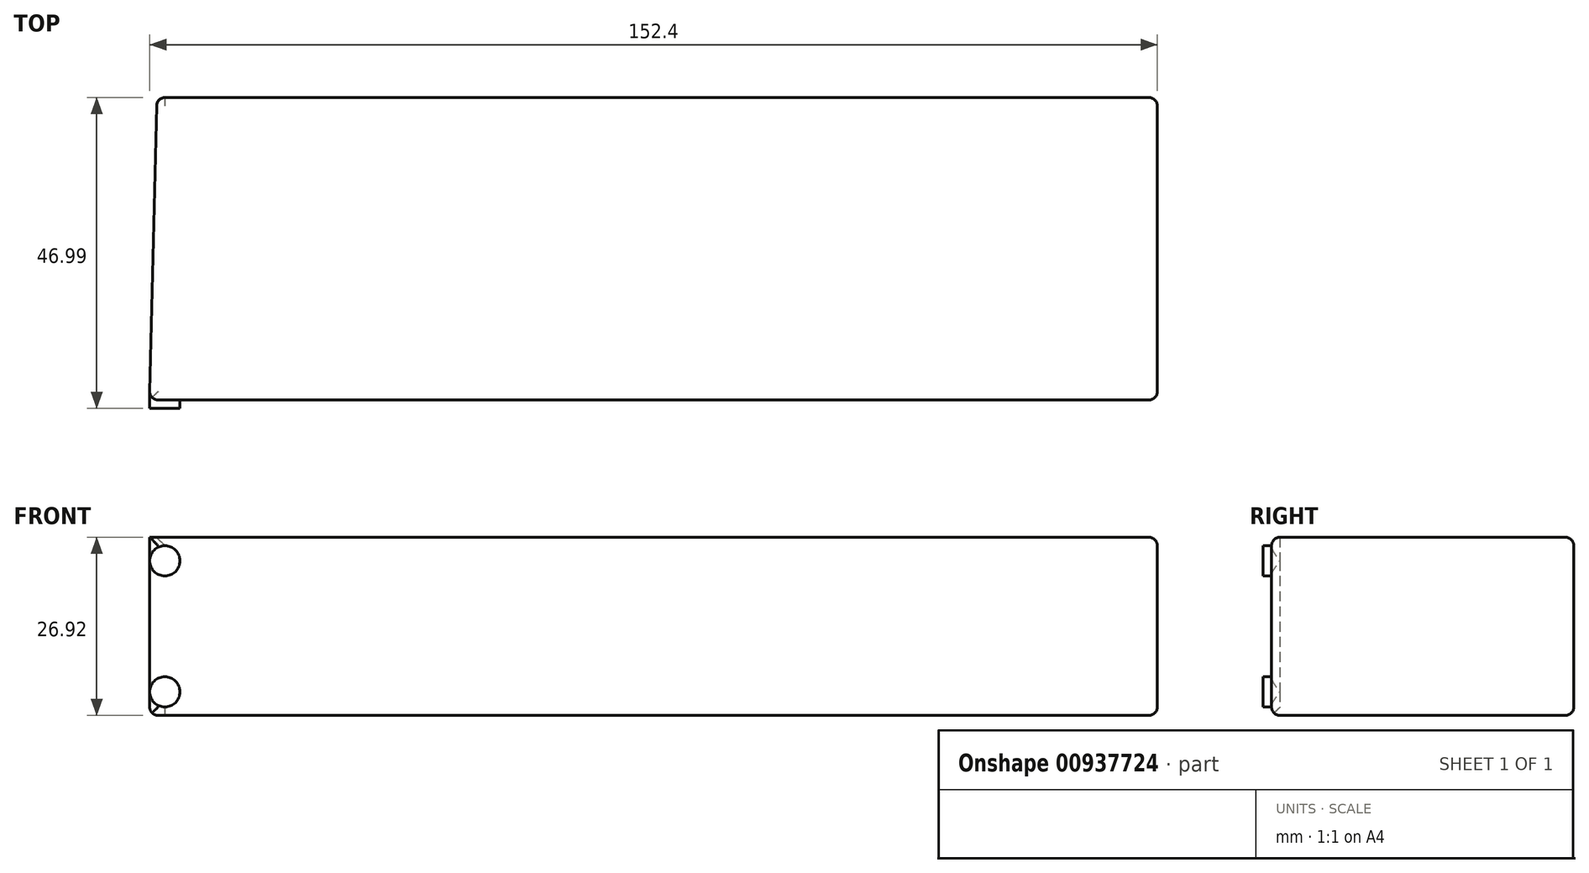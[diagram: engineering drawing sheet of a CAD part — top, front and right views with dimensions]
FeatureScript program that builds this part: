
annotation { "Feature Type Name" : "Feature", "Feature Type Description" : "" }
export const myFeature = defineFeature(function(context is Context, id is Id, definition is map)
    precondition{}
    {
        {
            var Q0;
            Q0=qCreatedBy(makeId("Right.planeOp"),FACE);
            var sketch = newSketch(context, id + "F0", { "sketchPlane" : qUnion([Q0])});
            skLineSegment(sketch, "E0.bottom", {"start": v(-22.86, 13.46) * mm, "end": v(22.86, 13.46) * mm});
            skLineSegment(sketch, "E0.top", {"start": v(-22.86, -13.46) * mm, "end": v(22.86, -13.46) * mm});
            skLineSegment(sketch, "E0.left", {"start": v(-22.86, 13.46) * mm, "end": v(-22.86, -13.46) * mm});
            skLineSegment(sketch, "E0.right", {"start": v(22.86, 13.46) * mm, "end": v(22.86, -13.46) * mm});
            skLineSegment(sketch, "E1", {"start": v(22.86, -13.46) * mm, "end": v(-22.86, 13.46) * mm, "construction": true});
            skLineSegment(sketch, "E2", {"start": v(22.86, 13.46) * mm, "end": v(-22.86, -13.46) * mm, "construction": true});
            skSolve(sketch);
        }
        {
            var Q0;
            Q0=makeQuery(id+"F0.imprint","IMPRINT",FACE,{"disambiguationData":[TD([[makeQuery(id+"F0.imprint","IMPRINT",EDGE,{"derivedFrom":sQuery(id+"F0.wireOp",EDGE,"E0.bottom")}),-1.0]])]});
            extrude(context, id + "F1", {"entities" : qUnion([Q0]), "endBound" : BoundingType.SYMMETRIC, "depth" : 152.4 * mm, "offsetDistance" : 25.4 * mm});
        }
        {
            var Q0;
            Q0=makeQuery(id+"F1.opExtrude","SWEPT_FACE",FACE,{"disambiguationData":[OSD([sQuery(id+"F0.wireOp",EDGE,"E0.left")])]});
            var Q1;
            Q1=makeQuery(id+"F1.opExtrude","SWEPT_FACE",FACE,{"disambiguationData":[OSD([sQuery(id+"F0.wireOp",EDGE,"E0.right")])]});
            var Q2;
            Q2=makeQuery(id+"F1.opExtrude","CAP_EDGE",EDGE,{"disambiguationData":[OSD([sQuery(id+"F0.wireOp",EDGE,"E0.bottom")])],"isStart":false});
            var Q3;
            Q3=makeQuery(id+"F1.opExtrude","CAP_EDGE",EDGE,{"disambiguationData":[OSD([sQuery(id+"F0.wireOp",EDGE,"E0.top")])],"isStart":false});
            fillet(context, id + "F2", {"entities" : qUnion([Q0, Q1, Q2, Q3]), "radius" : 1.27 * mm, "tangentPropagation" : true, "allowEdgeOverflow" : false});
        }
        {
            var Q0;
            Q0=makeQuery(id+"F1.opExtrude","SWEPT_FACE",FACE,{"disambiguationData":[OSD([sQuery(id+"F0.wireOp",EDGE,"E0.bottom")])]});
            var sketch = newSketch(context, id + "F3", { "sketchPlane" : qUnion([Q0])});
            skLineSegment(sketch, "E3.0.0", {"start": v(74.93, 22.86) * mm, "end": v(-74.93, 22.86) * mm, "construction": true});
            skLineSegment(sketch, "E3.0.2", {"start": v(-74.93, 22.86) * mm, "end": v(74.93, 22.86) * mm, "construction": true});
            skLineSegment(sketch, "E4.0.0", {"start": v(74.93, -22.86) * mm, "end": v(-74.93, -22.86) * mm, "construction": true});
            skLineSegment(sketch, "E4.0.2", {"start": v(-74.93, -22.86) * mm, "end": v(74.93, -22.86) * mm, "construction": true});
            skArc(sketch, "E5.0.0", {"start": v(-74.93, -22.86) * mm, "mid": v(-75.83, -22.49) * mm, "end": v(-76.2, -21.59) * mm, "construction": true});
            skArc(sketch, "E5.0.2", {"start": v(-76.2, -21.59) * mm, "mid": v(-75.83, -22.49) * mm, "end": v(-74.93, -22.86) * mm, "construction": true});
            skLineSegment(sketch, "E6.0.0", {"start": v(-76.2, -21.59) * mm, "end": v(-76.2, 21.59) * mm, "construction": true});
            skLineSegment(sketch, "E6.0.2", {"start": v(-76.2, 21.59) * mm, "end": v(-76.2, -21.59) * mm, "construction": true});
            skArc(sketch, "E7.0.0", {"start": v(-76.2, 21.6) * mm, "mid": v(-75.83, 22.49) * mm, "end": v(-74.93, 22.86) * mm, "construction": true});
            skArc(sketch, "E7.0.2", {"start": v(-76.2, 21.59) * mm, "mid": v(-75.83, 22.49) * mm, "end": v(-74.93, 22.86) * mm, "construction": true});
            skArc(sketch, "E8.0.2", {"start": v(-76.2, 21.59) * mm, "mid": v(-75.83, 22.49) * mm, "end": v(-74.93, 22.86) * mm});
            skLineSegment(sketch, "E9.0.0", {"start": v(76.2, -21.6) * mm, "end": v(76.2, 21.59) * mm, "construction": true});
            skLineSegment(sketch, "E9.0.2", {"start": v(76.2, 21.6) * mm, "end": v(76.2, -21.59) * mm, "construction": true});
            skArc(sketch, "E10.0.0", {"start": v(74.93, 22.86) * mm, "mid": v(75.83, 22.49) * mm, "end": v(76.2, 21.6) * mm, "construction": true});
            skArc(sketch, "E10.0.2", {"start": v(76.2, 21.59) * mm, "mid": v(75.83, 22.49) * mm, "end": v(74.93, 22.86) * mm, "construction": true});
            skArc(sketch, "E11.0.0", {"start": v(76.2, -21.59) * mm, "mid": v(75.83, -22.49) * mm, "end": v(74.93, -22.86) * mm, "construction": true});
            skArc(sketch, "E11.0.2", {"start": v(74.93, -22.86) * mm, "mid": v(75.83, -22.49) * mm, "end": v(76.2, -21.59) * mm, "construction": true});
            skLineSegment(sketch, "E12", {"start": v(-75.13, 22.86) * mm, "end": v(-76.2, -21.6) * mm});
            skSolve(sketch);
        }
        {
            var Q0;
            {var subQ1=sQuery(id+"F0.wireOp",EDGE,"E0.bottom");var subQ2=makeQuery(id+"F1.opExtrude","CAP_EDGE",EDGE,{"disambiguationData":[OSD([subQ1])],"isStart":true});Q0=makeQuery(id+"F3.imprint","IMPRINT",FACE,{"disambiguationData":[TD([[makeQuery(id+"F3.imprint","IMPRINT",EDGE,{"derivedFrom":subQ2}),-1.0]])]});}
            var Q1;
            {var subQ0=sQuery(id+"F3.wireOp",EDGE,"E8.0.2");var subQ4=sQuery(id+"F3.wireOp",EDGE,"E12");var subQ5=makeQuery(id+"F3.imprint","INTERSECT",VERTEX,{"derivedFrom":[subQ0,subQ4]});Q1=makeQuery(id+"F3.imprint","IMPRINT",FACE,{"disambiguationData":[TD([[makeQuery(id+"F3.imprint","IMPRINT",EDGE,{"disambiguationData":[TD([[subQ5,-1.0]])],"derivedFrom":subQ4}),-1.0]])]});}
            extrude(context, id + "F4", {"entities" : qUnion([Q0, Q1]), "operationType" : NewBodyOperationType.REMOVE, "endBound" : BoundingType.THROUGH_ALL, "oppositeDirection" : true, "depth" : 25.4 * mm, "offsetDistance" : 25.4 * mm});
        }
        {
            var Q0;
            Q0=makeQuery(id+"F4.boolean.opBoolean","COPY",EDGE,{"derivedFrom":makeQuery(id+"F4.opExtrude","SWEPT_EDGE",EDGE,{"disambiguationData":[OSD([sQuery(id+"F3.wireOp",EDGE,"E8.0.2"),sQuery(id+"F3.wireOp",EDGE,"E12")])]})});
            var Q1;
            Q1=makeQuery(id+"F4.boolean.opBoolean","COPY",EDGE,{"derivedFrom":makeQuery(id+"F4.opExtrude","CAP_EDGE",EDGE,{"disambiguationData":[OSD([sQuery(id+"F3.wireOp",EDGE,"E12")])],"isStart":true})});
            var Q2;
            Q2=makeQuery(id+"F4.boolean.opBoolean","INTERSECT",EDGE,{"derivedFrom":[makeQuery(id+"F1.opExtrude","SWEPT_FACE",FACE,{"disambiguationData":[OSD([sQuery(id+"F0.wireOp",EDGE,"E0.top")])]}),makeQuery(id+"F4.opExtrude","SWEPT_FACE",FACE,{"disambiguationData":[OSD([sQuery(id+"F3.wireOp",EDGE,"E12")])]})]});
            fillet(context, id + "F5", {"entities" : qUnion([Q0, Q1, Q2]), "radius" : 1.27 * mm, "tangentPropagation" : true, "allowEdgeOverflow" : false});
        }
        {
            var Q0;
            Q0=makeQuery(id+"F1.opExtrude","SWEPT_FACE",FACE,{"disambiguationData":[OSD([sQuery(id+"F0.wireOp",EDGE,"E0.left")])]});
            var sketch = newSketch(context, id + "F6", { "sketchPlane" : qUnion([Q0])});
            skCircle(sketch, "E13", {"center": v(-73.91, 9.9) * mm, "radius": 2.29 * mm});
            skCircle(sketch, "E14", {"center": v(-73.91, -9.9) * mm, "radius": 2.29 * mm});
            skSolve(sketch);
        }
        {
            var Q0;
            {var subQ0=sQuery(id+"F6.wireOp",EDGE,"E13");var subQ1=sQuery(id+"F0.wireOp",EDGE,"E0.left");var subQ2=makeQuery(id+"F1.opExtrude","SWEPT_FACE",FACE,{"disambiguationData":[OSD([subQ1])]});var subQ3=makeQuery(id+"F2.opFillet","BLEND_EDGE",EDGE,{"blendedFrom":[makeQuery(id+"F1.opExtrude","CAP_EDGE",EDGE,{"disambiguationData":[OSD([subQ1])],"isStart":true}),subQ2],"blendedInto":[subQ2]});var subQ4=makeQuery(id+"F6.imprint","INTERSECT",VERTEX,{"disambiguationData":[OD(0.0)],"derivedFrom":[subQ3,subQ0]});Q0=makeQuery(id+"F6.imprint","IMPRINT",FACE,{"disambiguationData":[TD([[makeQuery(id+"F6.imprint","IMPRINT",EDGE,{"disambiguationData":[TD([[subQ4,1.0]])],"derivedFrom":subQ0}),1.0]])]});}
            var Q1;
            {var subQ0=sQuery(id+"F6.wireOp",EDGE,"E14");var subQ1=sQuery(id+"F0.wireOp",EDGE,"E0.left");var subQ2=makeQuery(id+"F2.opFillet","BLEND_EDGE",EDGE,{"blendedFrom":[makeQuery(id+"F1.opExtrude","CAP_EDGE",EDGE,{"disambiguationData":[OSD([subQ1])],"isStart":true}),makeQuery(id+"F1.opExtrude","SWEPT_FACE",FACE,{"disambiguationData":[OSD([subQ1])]})],"blendedInto":[makeQuery(id+"F1.opExtrude","SWEPT_FACE",FACE,{"disambiguationData":[OSD([subQ1])]})]});var subQ3=makeQuery(id+"F6.imprint","INTERSECT",VERTEX,{"disambiguationData":[OD(0.0)],"derivedFrom":[subQ2,subQ0]});Q1=makeQuery(id+"F6.imprint","IMPRINT",FACE,{"disambiguationData":[TD([[makeQuery(id+"F6.imprint","IMPRINT",EDGE,{"disambiguationData":[TD([[subQ3,1.0]])],"derivedFrom":subQ0}),1.0]])]});}
            var Q2;
            {var subQ0=sQuery(id+"F6.wireOp",EDGE,"E14");var subQ1=sQuery(id+"F0.wireOp",EDGE,"E0.left");var subQ2=makeQuery(id+"F1.opExtrude","SWEPT_FACE",FACE,{"disambiguationData":[OSD([subQ1])]});var subQ3=makeQuery(id+"F2.opFillet","BLEND_EDGE",EDGE,{"blendedFrom":[makeQuery(id+"F1.opExtrude","CAP_EDGE",EDGE,{"disambiguationData":[OSD([subQ1])],"isStart":true}),subQ2],"blendedInto":[subQ2]});var subQ4=makeQuery(id+"F6.imprint","INTERSECT",VERTEX,{"disambiguationData":[OD(0.0)],"derivedFrom":[subQ3,subQ0]});Q2=makeQuery(id+"F6.imprint","IMPRINT",FACE,{"disambiguationData":[TD([[makeQuery(id+"F6.imprint","IMPRINT",EDGE,{"disambiguationData":[TD([[subQ4,-1.0]])],"derivedFrom":subQ0}),1.0]])]});}
            var Q3;
            {var subQ0=sQuery(id+"F6.wireOp",EDGE,"E13");var subQ1=sQuery(id+"F0.wireOp",EDGE,"E0.left");var subQ2=makeQuery(id+"F2.opFillet","BLEND_EDGE",EDGE,{"blendedFrom":[makeQuery(id+"F1.opExtrude","CAP_EDGE",EDGE,{"disambiguationData":[OSD([subQ1])],"isStart":true}),makeQuery(id+"F1.opExtrude","SWEPT_FACE",FACE,{"disambiguationData":[OSD([subQ1])]})],"blendedInto":[makeQuery(id+"F1.opExtrude","SWEPT_FACE",FACE,{"disambiguationData":[OSD([subQ1])]})]});var subQ3=makeQuery(id+"F6.imprint","INTERSECT",VERTEX,{"disambiguationData":[OD(0.0)],"derivedFrom":[subQ2,subQ0]});Q3=makeQuery(id+"F6.imprint","IMPRINT",FACE,{"disambiguationData":[TD([[makeQuery(id+"F6.imprint","IMPRINT",EDGE,{"disambiguationData":[TD([[subQ3,-1.0]])],"derivedFrom":subQ0}),1.0]])]});}
            extrude(context, id + "F7", {"entities" : qUnion([Q0, Q1, Q2, Q3]), "operationType" : NewBodyOperationType.ADD, "depth" : 1.27 * mm, "offsetDistance" : 25.4 * mm, "hasSecondDirection" : true, "secondDirectionOppositeDirection" : true, "secondDirectionDepth" : 1.27 * mm});
        }
    });
